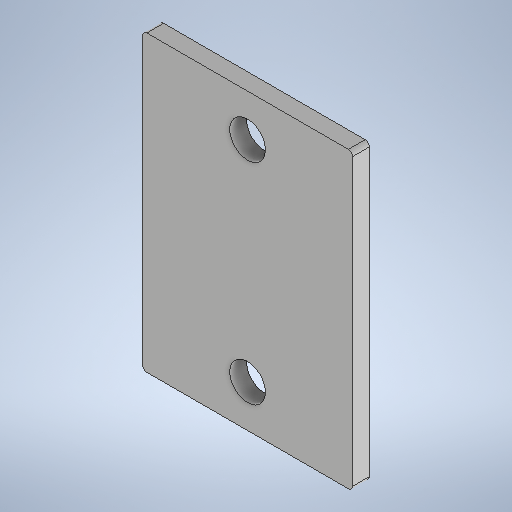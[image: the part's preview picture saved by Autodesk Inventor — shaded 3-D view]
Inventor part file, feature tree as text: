
AUTODESK INVENTOR PART (.ipt)
format: ipt  version: 2025 (Build 290162010, 162A)  size: 269,824 bytes
history: native  units: mm
features: sketch x2, other x2, sheet_metal_op x1, hole x1, fillet x1
ambient origin geometry x8: Origin, YZ Plane, XZ Plane, XY Plane, X Axis, Y Axis, Z Axis, Center Point
bodies: Solid1 (feature_tree)
feature tree (7):
  sheet_metal_op  "Face1"
  hole  "Hole1"  [1 undecoded]
  fillet  "Fillet1"  Radius=8.0mm
  sketch  "Sketch1"  dims[d0=100.0mm d1=140.0mm d2=8.0mm]
  other  "Plate1"
  sketch  "Sketch2"  dims[d3=17.0mm d4=6.0mm d5=4.0mm d6=2.0mm d7=90.0deg d8=8.0mm d9=20.594885mm d16=2.0mm d17=100.0mm]
  other  "Definition1"
note: 1 required parameter value undecoded (feature->parameter linkage not recoverable at this tier; creation-order binding heuristic only, values carry confidence <= 0.55)
